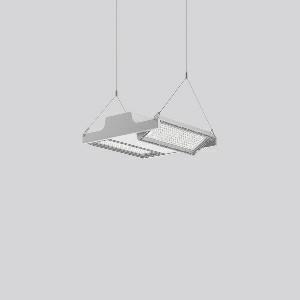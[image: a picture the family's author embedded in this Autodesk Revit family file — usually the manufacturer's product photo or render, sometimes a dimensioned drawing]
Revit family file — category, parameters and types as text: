
# Revit family: light_case_921682_004_1_76_1dbd
name_source: partatom
category: Lighting Fixtures
units: mm (PartAtom-declared; Revit-internal decimal feet)

## family parameters
Cut with Voids When Loaded = No
Host = Face
Light Source = No
Part Type = Normal
Room Calculation Point = No
Round Connector Dimension = Use Diameter
Shared = No

## types (1)
- LIGHT CASE (1 x LED Modul 865, 8700 lm, 6500)
    Apparent Load = 117 VA
    CIE Flux Codes = 80 98 100 100 100
    Color Rendering = 80
    Color Temperature = 6500
    Default Elevation = 1800 mm
    Description = Series: LIGHT CASE
Flat highbay luminaire for chain or cable suspension with 2 LED modules that can be swivelled. Housing: die cast aluminium and sheet steel, powder-coated. Optimised thermal management thanks to special luminaire design. Self-cleaning heat sink for constant heat dissipation. Cover: plastic (polycarbonate, shockproof), with integrated four-row lens system. LED modules can be swivelled ± 30° for optimum illumination. Suitable for chain or steel cable suspension (to be provided on site). With 5-pin connection terminal (1.5 m). With integrated movement sensor and light sensor for daylight detection on request. Ball impact proof in accordance with DIN 18032-03 (except steel cable suspension). Luminaire with limited surface temperature in accordance with EN 60598-2-24 for use in environments in which a deposit of conductive dust on the luminaire can be expected. 
Colour: silver, matt (approx. RAL 9006)
Length: 406 mm
Width: 397 mm
Height: 110 mm
Lamp: LED
Socket: without socket
Colour temperature: 6500K
Colour rendering index (CRI): 80
System power: 117 W
Rated luminous flux: 17400 lm
Luminous efficiency: 149 lm/W
Control gear: Converter, dimmable, DALI
Protection class: I
Type of protection: IP 65
    Height = 110 mm
    Lamp = 1 x LED Modul 865
    Lamp Light Flux = 8700 lm
    Lamp count = 1
    Length = 406 mm
    Lifetime = 50000 h
    Luminous efficacy = 149 lm/W
    Manufacturer = RZB
    ModVariant = No
    Model = 921682.004.1.76
    Mounting Place = Ceiling
    Mounting Type = Pendant
    Number of Poles = 1
    OnlyDefault = Yes
    Power Factor = 1
    Product Name = LIGHT CASE
    Product group = Pendant commercial luminaires
    ProductGroupID = 903
    Protection Class = Protection class I
    Protection Degree = IP 65
    RLX_Detail_Level = 1
    RLX_Emergency_Light_Flux = 0 lm
    RLX_Emergency_Type = 0
    RLX_Emergency_Type_DB = No
    RlxData = <blob elided: 24833 chars, md5=62e0682b>
    Socket = socket
    Standby Power = 0 W
    System Light Flux = 17400 lm
    System Power = 117 W
    Type Comments = Product without accessories
    Type Image = 921517.004.76.jpg
    URL = http://relux.com
    VarID = ---
    Voltage = 230 V
    Voltage Range = 220-240 V
    Weight = 0.00 kg
    Width = 397 mm

## geometry (parser evidence)
native form markers: Blend x4, Sweep x16
no freeform markers — native parametric forms only
